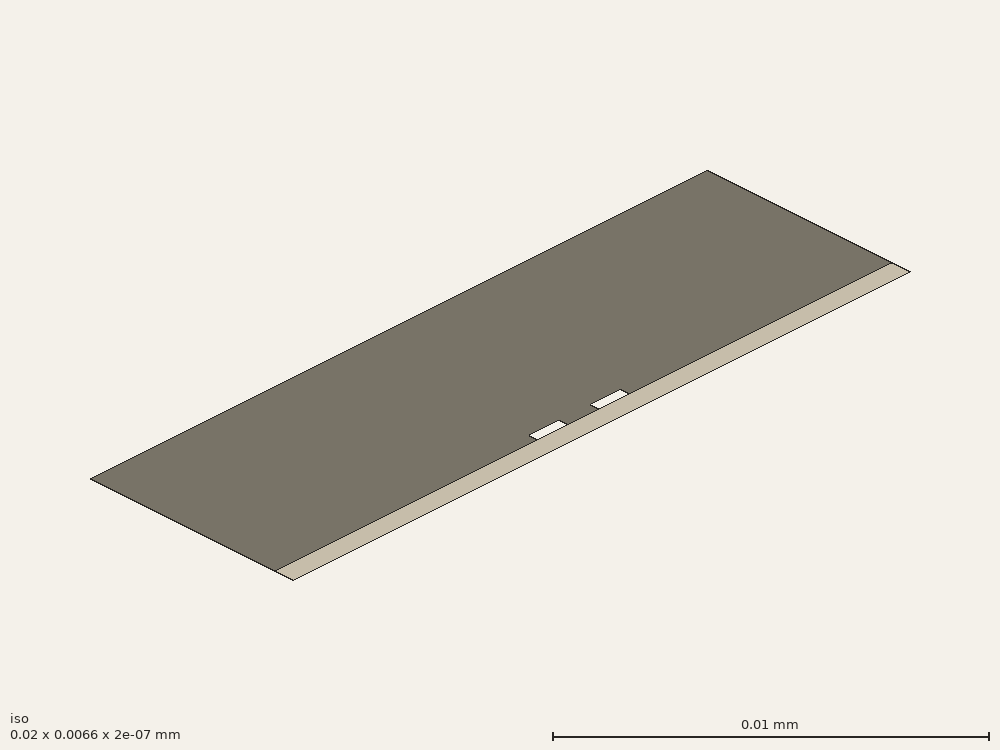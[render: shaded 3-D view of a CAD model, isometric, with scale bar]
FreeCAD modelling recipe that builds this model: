
FCSTD DOCUMENT  (FreeCAD 0.21R33694 (Git))
Label: diffPair
License: All rights reserved
LicenseURL: http://en.wikipedia.org/wiki/All_rights_reserved
objects: Part::Part2DObjectPython×6, App::FeaturePython×4, Part::FeaturePython×2
note: 8 computed .brp shape members not serialized (recipe doc carries the construction recipe); baked Part::Feature solids carry a one-line shape summary decoded from their .brp

FEATURE [Part::Part2DObjectPython] Rectangle  label="substrate"  # Draft 2D object (typed FeaturePython)
  Area = 12.7
  ChamferSize = 0
  Columns = 1
  FilletRadius = 0
  Height = 0.635
  Length = 20
  MakeFace = true
  Placement = pos=(-10,0,0) rot=(0,0,1;0rad)
  Rows = 1
FEATURE [Part::Part2DObjectPython] Wire  label="air"  # Draft 2D object (typed FeaturePython)
  Area = 119.4
  ChamferSize = 0
  Closed = true
  End = (-1.5,0.635,0)
  FilletRadius = 0
  Length = 53.2
  MakeFace = true
  Placement = pos=(-10,0.635,0) rot=(0,0,1;0rad)
  Points = (12) [(0,0,0),(0,6,0),(20,6,0),(20,-6.66134e-16,0),(11.5,-3.33067e-16,0),(11.5,0.3,0),(10.5,0.3,0),(10.5,-3.33067e-16,0),(9.5,-3.33067e-16,0),(9.5,0.3,0),(8.5,0.3,0),(8.5,-3.33067e-16,0)]
  Start = (-10,0.635,0)
  Subdivisions = 0
FEATURE [Part::FeaturePython] BooleanFragments  # WARN: FeaturePython — macro-defined, semantics opaque (R4)
  Mode = 0
  Objects = -> [Rectangle,Wire]
  Tolerance = 0
FEATURE [Part::FeaturePython] Clone  label="scaled to mm"  # Draft clone (typed FeaturePython)
  AttacherType = Attacher::AttachEngine3D
  Fuse = false
  Objects = -> [BooleanFragments]
  Scale = (0.001,0.001,1)
FEATURE [Part::Part2DObjectPython] Line  label="_PV1"  # Draft 2D object (typed FeaturePython)
  Area = 0
  ChamferSize = 0
  Closed = false
  End = (-0.001,0,0)
  FilletRadius = 0
  Length = 0.000635
  MakeFace = false
  Placement = pos=(-0.003,0.000635,0) rot=(0,0,1;0rad)
  Points = (2) [(0.002,0,0),(0.002,-0.000635,0)]
  Start = (-0.001,0.000635,0)
  Subdivisions = 0
FEATURE [Part::Part2DObjectPython] Line001  label="_PV2"  # Draft 2D object (typed FeaturePython)
  Area = 0
  ChamferSize = 0
  Closed = false
  End = (0.001,0,0)
  FilletRadius = 0
  Length = 0.000635
  MakeFace = true
  Placement = pos=(0.001,0.000635,0) rot=(0,0,1;0rad)
  Points = (2) [(0,0,0),(0,-0.000635,0)]
  Start = (0.001,0.000635,0)
  Subdivisions = 0
FEATURE [Part::Part2DObjectPython] Rectangle003  label="_Pline1"  # Draft 2D object (typed FeaturePython)
  Area = 0
  ChamferSize = 0
  Columns = 1
  FilletRadius = 0
  Height = 0.0003
  Length = 0.001
  MakeFace = false
  Placement = pos=(-0.0015,0.000635,0) rot=(0,0,1;0rad)
  Rows = 1
FEATURE [Part::Part2DObjectPython] Rectangle002  label="_Pline2"  # Draft 2D object (typed FeaturePython)
  Area = 0
  ChamferSize = 0
  Columns = 1
  FilletRadius = 0
  Height = 0.0003
  Length = 0.001
  MakeFace = false
  Placement = pos=(0.0005,0.000635,0) rot=(0,0,1;0rad)
  Rows = 1
FEATURE [App::FeaturePython] Text  label="_M1(current){line1,line2}"  # WARN: FeaturePython — macro-defined, semantics opaque (R4)
  Placement = pos=(-0.00185272,-0.00154398,0) rot=(0,0,1;0rad)
  Text = .
FEATURE [App::FeaturePython] Text001  label="_M1(voltage,0.5){V1,V2}"  # WARN: FeaturePython — macro-defined, semantics opaque (R4)
  Placement = pos=(-0.00185272,-0.00154398,0) rot=(0,0,1;0rad)
  Text = .
FEATURE [App::FeaturePython] Text002  label="_M2(current,0.5){line1,-line2}"  # WARN: FeaturePython — macro-defined, semantics opaque (R4)
  Placement = pos=(-0.00185272,-0.00154398,0) rot=(0,0,1;0rad)
  Text = .
FEATURE [App::FeaturePython] Text003  label="_M2(voltage){V1,-V2}"  # WARN: FeaturePython — macro-defined, semantics opaque (R4)
  Placement = pos=(-0.00185272,-0.00154398,0) rot=(0,0,1;0rad)
  Text = .
